# Revit family: PARLÉ TCM-1 Pendant Microphone_rev2
name_source: partatom
category: Communication Devices
units: mm (PartAtom-declared; Revit-internal decimal feet)

## family parameters
Cut with Voids When Loaded = No
Host = Face
Maintain Annotation Orientation = No
Part Type = Normal
Room Calculation Point = Yes
Round Connector Dimension = Use Diameter
Shared = Yes

## types (4) — shared parameters
Connector = Custom 2-pin (cable length 10 feet [3 meters])
Default Elevation = 0' - 0"
Depth = 0' - 2 1/2"
Dynamic Range = 92dB, A-Weighted
Frequency Response = 150 Hz - 16 kHz: ± 3dB
Height = 0' - 2"
Manufacturer = Biamp Systems
Manufacturer URL = https://www.biamp.com
Maximum SPL (less than 1% THD) = 106dB
Microphone Technology = 8-Element Digital Array
Part Number = Parlé TCM-1
Polar Pattern = Beamformed
Product Documentation Link = https://downloads.biamp.com
Product Page URL = https://www.biamp.com
Room Acoustics Examples URL = https://support.biamp.com
SNR (at 1kHz 94dBSPL A-Weighted) = > 70dB
Trim = Stainless Steel, Brushed
Weight Product = 0.4
Width = 0' - 2 1/2"

## per-type parameters (varying)
| type | Cable Finish | Case Finish | Description | Mic Grille Finish | Model |
| PARLÉ™ TCM-1 Pendant Microphone - White | Plastic, Opaque White | Wear Resistant Textured White | Beamtracking Pendant Microphone (Mic only. Requires TCM-1 Network Box. See TCM-1/TCM1A/TCM-1EX Network Box for additional data. Refer to Network Box for package pricing). | Wear Resistant Textured White | Parlé TCM-1 - White |
| PARLÉ™ TCM-1EX Pendant Microphone - Black | Plastic, Opaque Black | Wear Resistant Textured Black | Beamtracking Pendant Expansion Microphone (Mic only. Must be used with TCM-1 mic system. Cost for expansion mic only) | Wear Resistant Textured Black | Parlé TCM-1EX - Black |
| PARLÉ™ TCM-1 Pendant Microphone - Black | Plastic, Opaque Black | Wear Resistant Textured Black | Beamtracking Pendant Microphone (Mic only. Requires TCM-1 Network Box. See TCM-1/TCM1A/TCM-1EX Network Box for additional data. Refer to Network Box for package pricing). | Wear Resistant Textured Black | Parlé TCM-1 - Black |
| PARLÉ™ TCM-1EX Pendant Microphone - White | Plastic, Opaque White | Wear Resistant Textured White | Beamtracking Pendant Expansion Microphone (Mic only. Must be used with TCM-1 mic system. Cost for expansion mic only) | Wear Resistant Textured White | Parlé TCM-1EX - White |

## geometry (parser evidence)
native form markers: Sweep x4
no freeform markers — native parametric forms only
